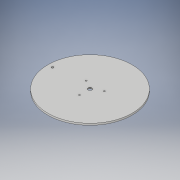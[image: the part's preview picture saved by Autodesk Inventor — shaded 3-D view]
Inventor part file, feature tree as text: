
AUTODESK INVENTOR PART (.ipt)
format: ipt  version: 2019 (Build 230136000, 136)  size: 131,584 bytes
history: native  units: mm
features: sketch x5, extrude x4, chamfer x1, hole x1
ambient origin geometry x8: Origin, YZ Plane, XZ Plane, XY Plane, X Axis, Y Axis, Z Axis, Center Point
bodies: Solide1 (feature_tree)
feature tree (11):
  extrude  "Extrusion1"  Depth=10.0mm
  extrude  "Extrusion2"  Depth=5.0mm TaperAngle=0.0deg
  extrude  "Extrusion3"  Depth=10.0mm
  chamfer  "Chanfrein1"  Distance=5.0mm
  hole  "Perçage1"  [1 undecoded]
  extrude  "Extrusion5"  Depth=2.0mm TaperAngle=0.0deg
  sketch  "Esquisse1"
  sketch  "Esquisse2"
  sketch  "Esquisse3"
  sketch  "Esquisse4"
  sketch  "Esquisse6"
note: 1 required parameter value undecoded (feature->parameter linkage not recoverable at this tier; creation-order binding heuristic only, values carry confidence <= 0.55)
